# Revit family: BE_50932.2_de_DE
name_source: partatom
category: Lighting Fixtures
units: mm (PartAtom-declared; Revit-internal decimal feet)

## family parameters
Cut with Voids When Loaded = Yes
Host = Face
Light Source = Yes
Part Type = Normal
Room Calculation Point = Yes
Round Connector Dimension = Use Diameter
Shared = No

## types (1)
- BEGA_50932.2_K3
    AC/DC = AC/DC
    Aktualisierung = 2022-12-01T04:00:03
    Apparent Load = 0 VA
    BEGA_Dummy = No
    BEGA_IES = Yes
    BEGA_Intern = Yes
    BEGA_Intern_Konstruktion = Yes
    BEGA_Intern_an = Yes
    BEGA_Intern_aus = Yes
    Befestigungsabstand = 66 mm
    Befestigungsbohrung = Ø 4,5 mm
    Beschreibung_Sonderanfertigung = Hier können Sie Informationen zur Sonderanfertigung eintragen.
    Bestellnummer = 50932.2K3
    CE_Konformität = ja
    Color Filter = 16777215
    Default Elevation = 0 mm  [stored 0 ft]
    Description = Deckenleuchte · Tiefstrahler
    Dimming Lamp Color Temperature Shift = <None>
    Energieeffizienzklasse = LED A++ - A
    Farbtemperatur = 3000 K
    Farbwiedergabeindex = CRI > 90
    Frequenz = 0/50-60 Hz
    Gewicht = 0.55 kg
    LED_Modulbezeichnung = LED-1029/930
    Lamp = LED 3.9 W
    Lampenlichtstrom = 525 lm
    Lastklassifizierung = Beleuchtung
    Lebensdauerkriterien = L70B50 @ 25 °C = 200000 h
    Leuchtenlichtstrom = 378 lm
    Logo = <None>
    M_A = No
    M_G = No
    M_W = No
    Manufacturer = BEGA
    Material_05 = BEGA_Oberfläche_Aluminium_Guss
    Material_13 = BEGA_Kunststoff_matt
    Material_15 = BEGA_Leuchtmedium_matt
    Material_17 = BEGA_Reflektor
    Material_22 = BEGA_Oberfläche_Aluminium_matt
    Material_23 = BEGA_Oberfläche_Chrom_poliert
    Material_34 = BEGA_Oberfläche_Samtweiss_matt
    Model = 50932.2K3
    Photometric Web File = BE_50932-2K3.ies
    Produktdatenblatt = https://cdn.bega.com
    Schutzart = IP 20
    Schutzklasse = I
    Sonderanfertigung = No
    Spannung = 240 V
    Strom = 0,35 A
    Tilt Angle = 0.00°
    URL = https://www.bega.com
    Umgebungstemperatur = 25 °C

note: [stored X ft] marks values corroborated as IEEE doubles in the binary element streams (Revit-internal decimal feet)
